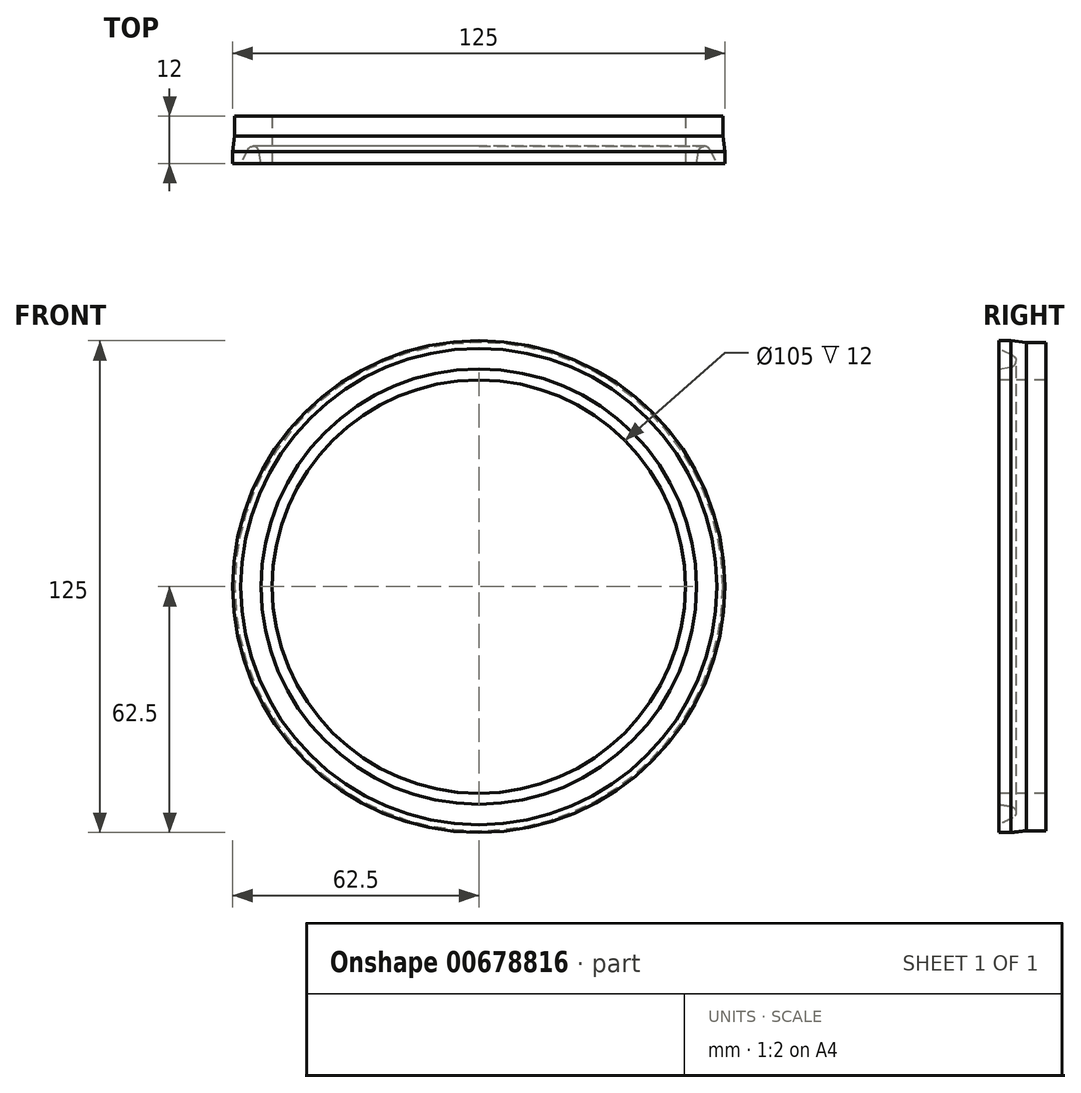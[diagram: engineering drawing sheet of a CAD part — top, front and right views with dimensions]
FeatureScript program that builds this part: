
annotation { "Feature Type Name" : "Feature", "Feature Type Description" : "" }
export const myFeature = defineFeature(function(context is Context, id is Id, definition is map)
    precondition{}
    {
        {
            var Q0;
            Q0=qCreatedBy(makeId("Right.planeOp"),FACE);
            var sketch = newSketch(context, id + "F0", { "sketchPlane" : qUnion([Q0])});
            skLineSegment(sketch, "E0", {"start": v(0, 52.5) * mm, "end": v(12, 52.5) * mm});
            skLineSegment(sketch, "E1", {"start": v(12, 52.5) * mm, "end": v(12, 62) * mm});
            skLineSegment(sketch, "E2", {"start": v(12, 62) * mm, "end": v(7, 62) * mm});
            skLineSegment(sketch, "E3", {"start": v(7, 62) * mm, "end": v(3, 62.5) * mm});
            skLineSegment(sketch, "E4", {"start": v(3, 62.5) * mm, "end": v(0, 62.5) * mm});
            skLineSegment(sketch, "E5", {"start": v(0, 62.5) * mm, "end": v(0, 60.5) * mm});
            skLineSegment(sketch, "E6", {"start": v(0, 60.5) * mm, "end": v(3.56, 58.68) * mm});
            skLineSegment(sketch, "E7", {"start": v(3.15, 55.87) * mm, "end": v(0, 55.3) * mm});
            skLineSegment(sketch, "E8", {"start": v(0, 55.3) * mm, "end": v(0, 52.5) * mm});
            skPoint(sketch, "E9.visualSharp", {"position": v(7.52, 56.66) * mm});
            skArc(sketch, "E9.filletArc", {"start": v(3.15, 55.87) * mm, "mid": v(4.37, 57.13) * mm, "end": v(3.56, 58.68) * mm});
            skSolve(sketch);
        }
        {
            var Q0;
            Q0=qCreatedBy(makeId("Right.planeOp"),FACE);
            var sketch = newSketch(context, id + "F1", { "sketchPlane" : qUnion([Q0])});
            skLineSegment(sketch, "E10", {"start": v(-35.82, 0) * mm, "end": v(41.07, 0) * mm});
            skSolve(sketch);
        }
        {
            var Q0;
            Q0=makeQuery(id+"F0.imprint","IMPRINT",FACE,{"disambiguationData":[TD([[makeQuery(id+"F0.imprint","IMPRINT",EDGE,{"derivedFrom":sQuery(id+"F0.wireOp",EDGE,"E0")}),1.0]])]});
            var Q1;
            Q1=sQuery(id+"F1.wireOp",EDGE,"E10");
            revolve(context, id + "F2", {"entities" : qUnion([Q0]), "axis" : qUnion([Q1]), "revolveType" : RevolveType.FULL});
        }
    });
